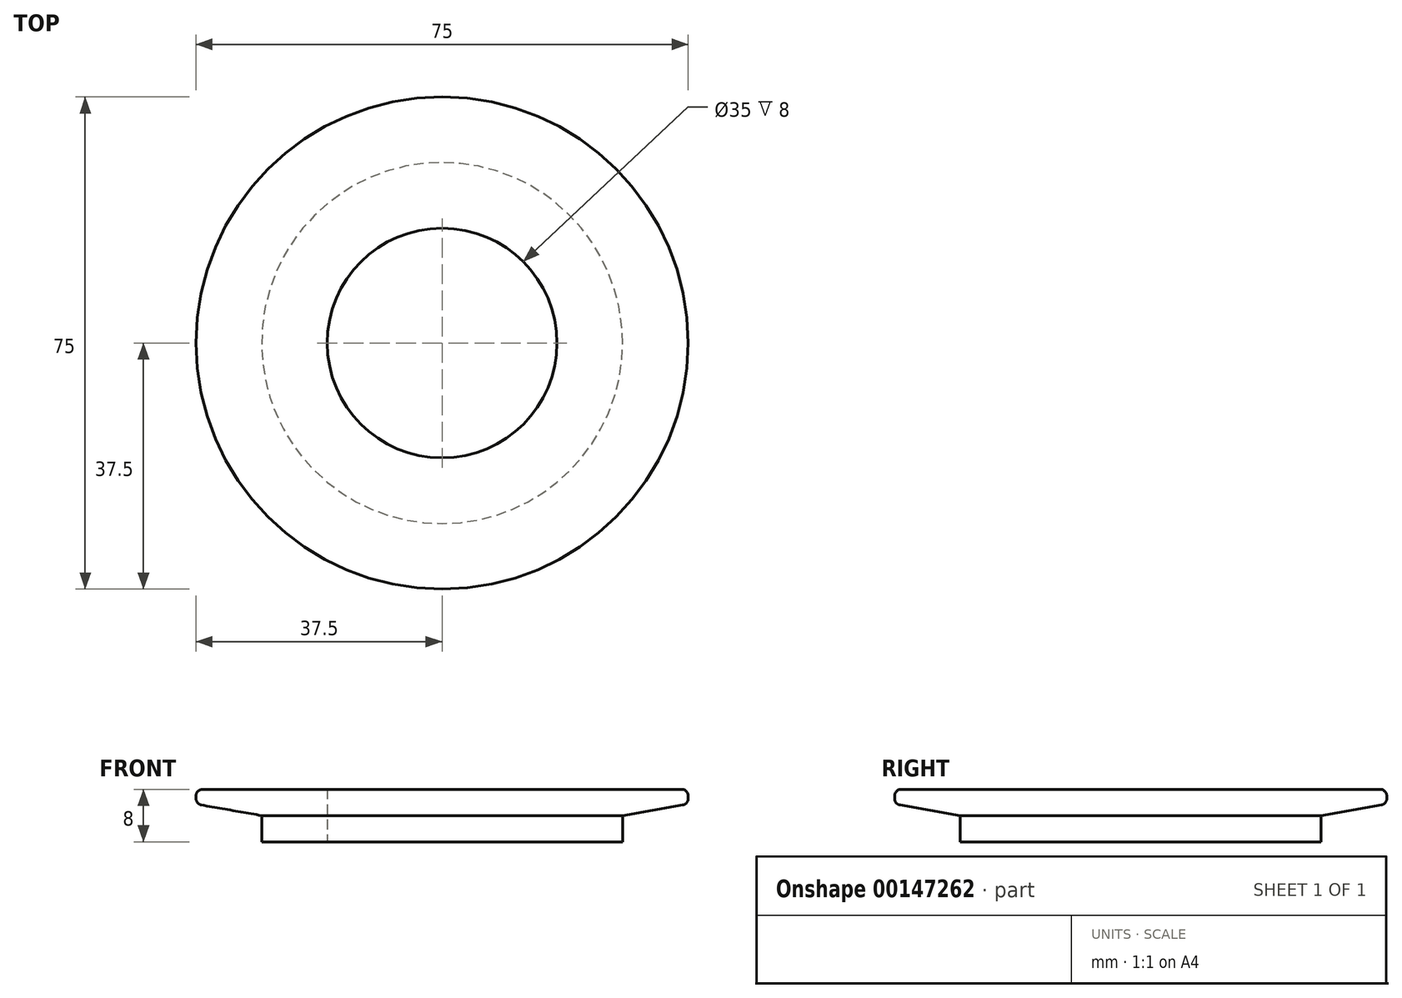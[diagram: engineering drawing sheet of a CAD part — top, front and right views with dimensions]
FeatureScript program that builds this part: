
annotation { "Feature Type Name" : "Feature", "Feature Type Description" : "" }
export const myFeature = defineFeature(function(context is Context, id is Id, definition is map)
    precondition{}
    {
        {
            var Q0;
            Q0=qCreatedBy(makeId("Right.planeOp"),FACE);
            var sketch = newSketch(context, id + "F0", { "sketchPlane" : qUnion([Q0])});
            skLineSegment(sketch, "E0", {"start": v(0, 0) * mm, "end": v(0, 8) * mm, "construction": true});
            skLineSegment(sketch, "E1", {"start": v(-37.5, 6.6) * mm, "end": v(-37.5, 7) * mm, "construction": true});
            skLineSegment(sketch, "E2", {"start": v(-27.5, 0) * mm, "end": v(-27.5, 8) * mm, "construction": true});
            skLineSegment(sketch, "E3", {"start": v(-27.5, 0) * mm, "end": v(-17.5, 0) * mm});
            skPoint(sketch, "E4", {"position": v(-17.5, 0) * mm});
            skLineSegment(sketch, "E5", {"start": v(-17.5, 0) * mm, "end": v(-17.5, 8) * mm});
            skLineSegment(sketch, "E6", {"start": v(-17.5, 8) * mm, "end": v(-36.5, 8) * mm});
            skLineSegment(sketch, "E7", {"start": v(-27.5, 0) * mm, "end": v(-27.5, 4) * mm});
            skLineSegment(sketch, "E8", {"start": v(-37.5, 8) * mm, "end": v(-37.5, 5.75) * mm});
            skLineSegment(sketch, "E9", {"start": v(-36.67, 5.6) * mm, "end": v(-27.5, 4) * mm});
            skPoint(sketch, "E10.visualSharp", {"position": v(-37.5, 8) * mm});
            skArc(sketch, "E10.filletArc", {"start": v(-36.5, 8) * mm, "mid": v(-37.2, 7.7) * mm, "end": v(-37.5, 7) * mm});
            skPoint(sketch, "E11.newPointB", {"position": v(-37.5, 0) * mm});
            skArc(sketch, "E11.filletArc", {"start": v(-37.5, 6.6) * mm, "mid": v(-37.27, 5.95) * mm, "end": v(-36.67, 5.6) * mm});
            skSolve(sketch);
        }
        {
            var Q0;
            Q0=makeQuery(id+"F0.imprint","IMPRINT",FACE,{"disambiguationData":[TD([[makeQuery(id+"F0.imprint","IMPRINT",EDGE,{"derivedFrom":sQuery(id+"F0.wireOp",EDGE,"E3")}),1.0]])]});
            var Q1;
            Q1=sQuery(id+"F0.wireOp",EDGE,"E0");
            revolve(context, id + "F1", {"entities" : qUnion([Q0]), "axis" : qUnion([Q1]), "revolveType" : RevolveType.FULL});
        }
    });
